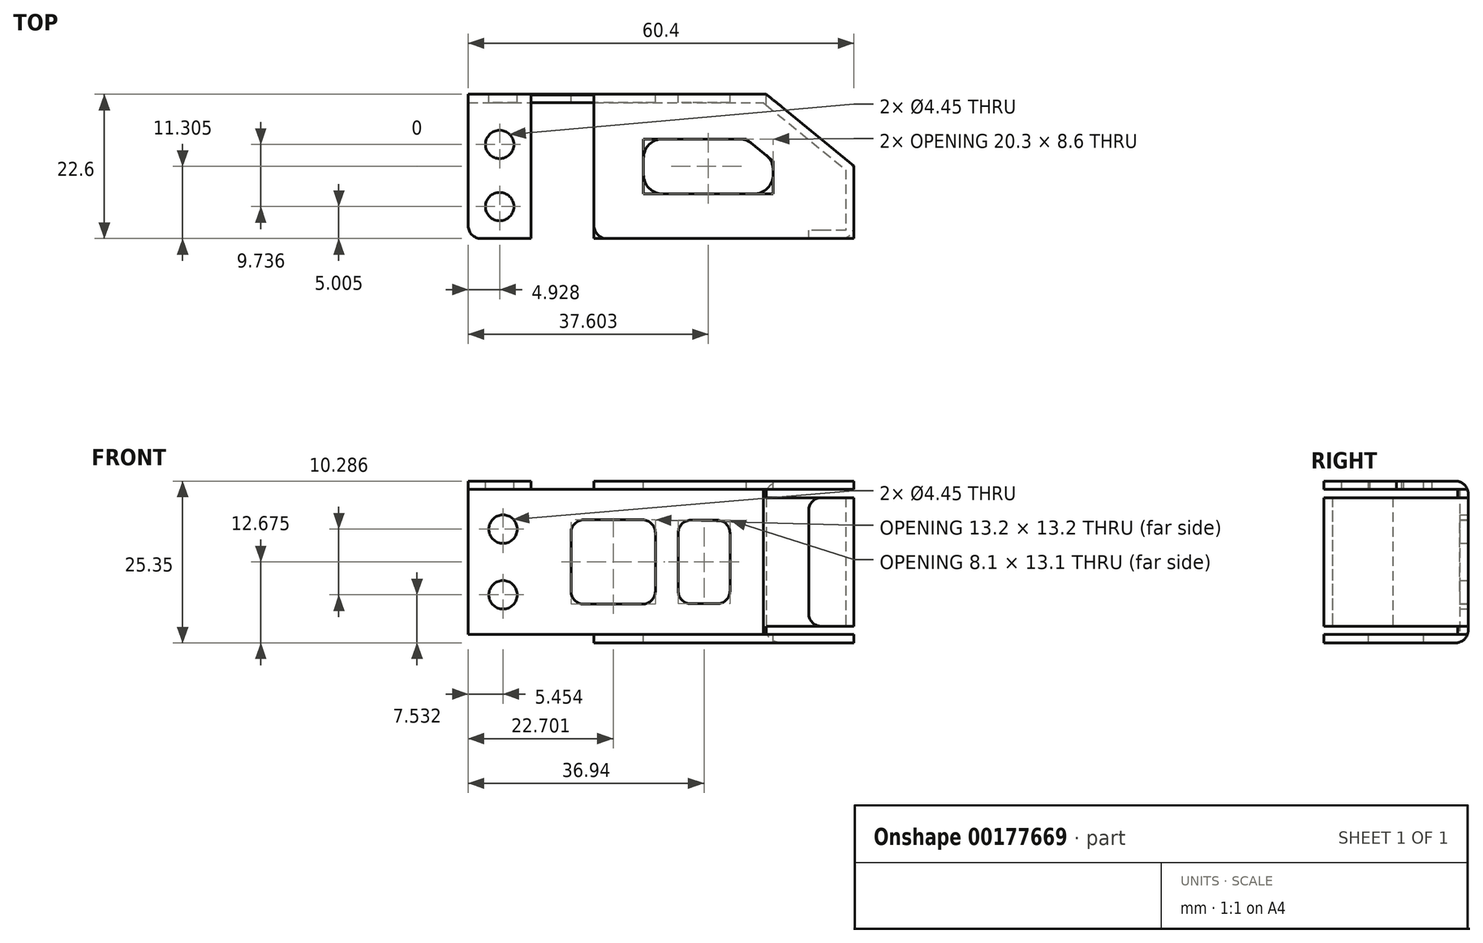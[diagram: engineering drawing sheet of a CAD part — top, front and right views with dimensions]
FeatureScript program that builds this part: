
annotation { "Feature Type Name" : "Feature", "Feature Type Description" : "" }
export const myFeature = defineFeature(function(context is Context, id is Id, definition is map)
    precondition{}
    {
        {
            var Q0;
            Q0=qCreatedBy(makeId("Top.planeOp"),FACE);
            var sketch = newSketch(context, id + "F0", { "sketchPlane" : qUnion([Q0])});
            skLineSegment(sketch, "E0.bottom", {"start": v(-31.59, -12.14) * mm, "end": v(13.31, -12.14) * mm});
            skLineSegment(sketch, "E0.top", {"start": v(-31.59, -33.44) * mm, "end": v(26.21, -33.44) * mm});
            skLineSegment(sketch, "E0.left", {"start": v(-31.59, -12.14) * mm, "end": v(-31.59, -33.44) * mm});
            skLineSegment(sketch, "E0.right", {"start": v(26.21, -22.66) * mm, "end": v(26.21, -33.44) * mm});
            skLineSegment(sketch, "E1", {"start": v(13.31, -12.14) * mm, "end": v(26.21, -22.66) * mm});
            skSolve(sketch);
        }
        {
            var Q0;
            Q0=makeQuery(id+"F0.imprint","IMPRINT",FACE,{"disambiguationData":[TD([[makeQuery(id+"F0.imprint","IMPRINT",EDGE,{"derivedFrom":sQuery(id+"F0.wireOp",EDGE,"E0.bottom")}),-1.0]])]});
            extrude(context, id + "F1", {"entities" : qUnion([Q0]), "depth" : 22.75 * mm});
        }
        {
            var Q0;
            Q0=makeQuery(id+"F1.opExtrude","SWEPT_FACE",FACE,{"disambiguationData":[OSD([sQuery(id+"F0.wireOp",EDGE,"E0.top")])]});
            shell(context, id + "F2", {"entities" : qUnion([Q0]), "thickness" : 1.3 * mm, "oppositeDirection" : true});
        }
        {
            var Q0;
            Q0=makeQuery(id+"F1.opExtrude","SWEPT_FACE",FACE,{"disambiguationData":[OSD([sQuery(id+"F0.wireOp",EDGE,"E0.left")])]});
            var sketch = newSketch(context, id + "F3", { "sketchPlane" : qUnion([Q0])});
            skLineSegment(sketch, "E2", {"start": v(12.14, -1.3) * mm, "end": v(12.14, 22.75) * mm});
            skLineSegment(sketch, "E3", {"start": v(12.14, 22.75) * mm, "end": v(33.44, 22.75) * mm});
            skSolve(sketch);
        }
        {
            var Q0;
            {var subQ0=sQuery(id+"F3.wireOp",EDGE,"E2");Q0=makeQuery(id+"F3.imprint","IMPRINT",FACE,{"disambiguationData":[TD([[makeQuery(id+"F3.imprint","IMPRINT",EDGE,{"derivedFrom":subQ0}),-1.0]])]});}
            extrude(context, id + "F4", {"entities" : qUnion([Q0]), "operationType" : NewBodyOperationType.REMOVE, "oppositeDirection" : true, "depth" : 19.7 * mm});
        }
        {
            var Q0;
            Q0=makeQuery(id+"F1.opExtrude","CAP_FACE",FACE,{"disambiguationData":[OSD([sQuery(id+"F0.wireOp",EDGE,"E0.bottom"),sQuery(id+"F0.wireOp",EDGE,"E0.top"),sQuery(id+"F0.wireOp",EDGE,"E0.left"),sQuery(id+"F0.wireOp",EDGE,"E0.right"),sQuery(id+"F0.wireOp",EDGE,"E1")])],"isStart":false});
            var sketch = newSketch(context, id + "F5", { "sketchPlane" : qUnion([Q0])});
            skLineSegment(sketch, "E4", {"start": v(-13.19, -12.14) * mm, "end": v(-13.19, -33.44) * mm});
            skLineSegment(sketch, "E5", {"start": v(-23.04, -33.44) * mm, "end": v(-23.04, -12.14) * mm});
            skLineSegment(sketch, "E6", {"start": v(-13.19, -33.44) * mm, "end": v(-32.89, -33.44) * mm});
            skLineSegment(sketch, "E7", {"start": v(-32.89, -33.44) * mm, "end": v(-23.04, -33.44) * mm});
            skLineSegment(sketch, "E8", {"start": v(-23.04, -12.14) * mm, "end": v(-32.89, -12.14) * mm});
            skLineSegment(sketch, "E9", {"start": v(-23.04, -12.14) * mm, "end": v(-23.04, -10.84) * mm});
            skLineSegment(sketch, "E10", {"start": v(-13.19, -12.14) * mm, "end": v(-13.19, -10.84) * mm});
            skSolve(sketch);
        }
        {
            var Q0;
            Q0=makeQuery(id+"F5.imprint","IMPRINT",FACE,{"disambiguationData":[TD([[makeQuery(id+"F5.imprint","IMPRINT",EDGE,{"derivedFrom":sQuery(id+"F5.wireOp",EDGE,"E4")}),-1.0]])]});
            extrude(context, id + "F6", {"entities" : qUnion([Q0]), "operationType" : NewBodyOperationType.REMOVE, "oppositeDirection" : true, "depth" : 1.3 * mm});
        }
        {
            var Q0;
            {var subQ0=sQuery(id+"F0.wireOp",EDGE,"E1");var subQ1=sQuery(id+"F0.wireOp",EDGE,"E0.top");var subQ2=sQuery(id+"F0.wireOp",EDGE,"E0.right");var subQ3=sQuery(id+"F0.wireOp",EDGE,"E0.bottom");Q0=makeQuery(id+"F6.boolean.opBoolean","SPLIT",FACE,{"disambiguationData":[TD([makeQuery(id+"F1.opExtrude","SWEPT_FACE",FACE,{"disambiguationData":[OSD([subQ2])]})])],"derivedFrom":makeQuery(id+"F1.opExtrude","CAP_FACE",FACE,{"disambiguationData":[OSD([subQ3,subQ1,sQuery(id+"F0.wireOp",EDGE,"E0.left"),subQ2,subQ0])],"isStart":false})});}
            var sketch = newSketch(context, id + "F7", { "sketchPlane" : qUnion([Q0])});
            skLineSegment(sketch, "E11", {"start": v(-5.44, -17.84) * mm, "end": v(10.65, -17.84) * mm});
            skLineSegment(sketch, "E12", {"start": v(10.65, -17.84) * mm, "end": v(14.86, -21.27) * mm});
            skLineSegment(sketch, "E13", {"start": v(14.86, -21.27) * mm, "end": v(14.86, -26.44) * mm});
            skLineSegment(sketch, "E14", {"start": v(14.86, -26.44) * mm, "end": v(-5.44, -26.44) * mm});
            skLineSegment(sketch, "E15", {"start": v(-5.44, -26.44) * mm, "end": v(-5.44, -17.84) * mm});
            skSolve(sketch);
        }
        {
            var Q0;
            Q0=makeQuery(id+"F7.imprint","IMPRINT",FACE,{"disambiguationData":[TD([[makeQuery(id+"F7.imprint","IMPRINT",EDGE,{"derivedFrom":sQuery(id+"F7.wireOp",EDGE,"E11")}),-1.0]])]});
            extrude(context, id + "F8", {"entities" : qUnion([Q0]), "operationType" : NewBodyOperationType.REMOVE, "oppositeDirection" : true, "depth" : 61.35 * mm});
        }
        {
            var Q0;
            Q0=makeQuery(id+"F1.opExtrude","SWEPT_FACE",FACE,{"disambiguationData":[OSD([sQuery(id+"F0.wireOp",EDGE,"E0.bottom")])]});
            var sketch = newSketch(context, id + "F9", { "sketchPlane" : qUnion([Q0])});
            skLineSegment(sketch, "E16.bottom", {"start": v(-8.1, 4.82) * mm, "end": v(0, 4.82) * mm});
            skLineSegment(sketch, "E16.top", {"start": v(-8.1, 17.93) * mm, "end": v(0, 17.93) * mm});
            skLineSegment(sketch, "E16.left", {"start": v(-8.1, 4.82) * mm, "end": v(-8.1, 17.93) * mm});
            skLineSegment(sketch, "E16.right", {"start": v(0, 4.82) * mm, "end": v(0, 17.93) * mm});
            skLineSegment(sketch, "E17.bottom", {"start": v(3.59, 4.77) * mm, "end": v(16.79, 4.77) * mm});
            skLineSegment(sketch, "E17.top", {"start": v(3.59, 17.97) * mm, "end": v(16.79, 17.97) * mm});
            skLineSegment(sketch, "E17.left", {"start": v(3.59, 4.77) * mm, "end": v(3.59, 17.98) * mm});
            skLineSegment(sketch, "E17.right", {"start": v(16.79, 4.77) * mm, "end": v(16.79, 17.97) * mm});
            skLineSegment(sketch, "E18", {"start": v(27.44, -1.3) * mm, "end": v(27.44, 24.05) * mm, "construction": true});
            skLineSegment(sketch, "E19", {"start": v(-13.78, 11.38) * mm, "end": v(32.89, 11.38) * mm, "construction": true});
            skCircle(sketch, "E20", {"center": v(27.44, 16.52) * mm, "radius": 2.23 * mm});
            skCircle(sketch, "E21", {"center": v(27.44, 6.23) * mm, "radius": 2.23 * mm});
            skLineSegment(sketch, "E22", {"start": v(27.44, 14.3) * mm, "end": v(27.44, 11.38) * mm});
            skLineSegment(sketch, "E23", {"start": v(27.44, 11.38) * mm, "end": v(27.44, 8.46) * mm});
            skLineSegment(sketch, "E24", {"start": v(13.19, -1.3) * mm, "end": v(13.19, 0) * mm});
            skLineSegment(sketch, "E25", {"start": v(13.19, 0) * mm, "end": v(32.89, 0) * mm});
            skPoint(sketch, "E26", {"position": v(16.79, 11.37) * mm});
            skPoint(sketch, "E27", {"position": v(0, 11.37) * mm});
            skSolve(sketch);
        }
        {
            var Q0;
            Q0=makeQuery(id+"F9.imprint","IMPRINT",FACE,{"disambiguationData":[TD([[makeQuery(id+"F9.imprint","IMPRINT",EDGE,{"derivedFrom":sQuery(id+"F9.wireOp",EDGE,"E16.bottom")}),1.0]])]});
            var Q1;
            Q1=makeQuery(id+"F9.imprint","IMPRINT",FACE,{"disambiguationData":[TD([[makeQuery(id+"F9.imprint","IMPRINT",EDGE,{"derivedFrom":sQuery(id+"F9.wireOp",EDGE,"E17.bottom")}),1.0]])]});
            var Q2;
            {var subQ0=sQuery(id+"F9.wireOp",EDGE,"E24");Q2=makeQuery(id+"F9.imprint","IMPRINT",FACE,{"disambiguationData":[TD([[makeQuery(id+"F9.imprint","IMPRINT",EDGE,{"derivedFrom":subQ0}),-1.0]])]});}
            var Q3;
            Q3=makeQuery(id+"F9.imprint","IMPRINT",FACE,{"disambiguationData":[TD([[makeQuery(id+"F9.imprint","IMPRINT",EDGE,{"derivedFrom":sQuery(id+"F9.wireOp",EDGE,"E21")}),1.0]])]});
            var Q4;
            Q4=makeQuery(id+"F9.imprint","IMPRINT",FACE,{"disambiguationData":[TD([[makeQuery(id+"F9.imprint","IMPRINT",EDGE,{"derivedFrom":sQuery(id+"F9.wireOp",EDGE,"E20")}),1.0]])]});
            extrude(context, id + "F10", {"entities" : qUnion([Q0, Q1, Q2, Q3, Q4]), "operationType" : NewBodyOperationType.REMOVE, "oppositeDirection" : true, "depth" : 25 * mm});
        }
        {
            var Q0;
            Q0=makeQuery(id+"F2.opShell","OFFSET_FACE",FACE,{"disambiguationData":[OSD([sQuery(id+"F0.wireOp",EDGE,"E0.right")])]});
            var sketch = newSketch(context, id + "F11", { "sketchPlane" : qUnion([Q0])});
            skLineSegment(sketch, "E28", {"start": v(32.14, 22.75) * mm, "end": v(32.14, 0) * mm});
            skSolve(sketch);
        }
        {
            var Q0;
            {var subQ0=sQuery(id+"F11.wireOp",EDGE,"E28");Q0=makeQuery(id+"F11.imprint","IMPRINT",FACE,{"disambiguationData":[TD([[makeQuery(id+"F11.imprint","IMPRINT",EDGE,{"derivedFrom":subQ0}),1.0]])]});}
            extrude(context, id + "F12", {"entities" : qUnion([Q0]), "operationType" : NewBodyOperationType.ADD, "depth" : 5.8 * mm});
        }
        {
            var Q0;
            Q0=makeQuery(id+"F1.opExtrude","SWEPT_FACE",FACE,{"disambiguationData":[OSD([sQuery(id+"F0.wireOp",EDGE,"E0.bottom")])]});
            var sketch = newSketch(context, id + "F13", { "sketchPlane" : qUnion([Q0])});
            skLineSegment(sketch, "E29", {"start": v(-13.78, 0) * mm, "end": v(-36.67, 0) * mm});
            skLineSegment(sketch, "E30", {"start": v(-13.78, 22.75) * mm, "end": v(-38.37, 22.75) * mm});
            skLineSegment(sketch, "E31", {"start": v(-13.78, 1.3) * mm, "end": v(-36.66, 1.3) * mm});
            skLineSegment(sketch, "E32", {"start": v(-13.78, 21.45) * mm, "end": v(-38.37, 21.45) * mm});
            skLineSegment(sketch, "E33", {"start": v(-36.67, 0) * mm, "end": v(-36.66, 1.3) * mm});
            skLineSegment(sketch, "E34", {"start": v(-38.37, 21.45) * mm, "end": v(-38.37, 22.75) * mm});
            skSolve(sketch);
        }
        {
            var Q0;
            {var subQ0=sQuery(id+"F13.wireOp",EDGE,"E29");Q0=makeQuery(id+"F13.imprint","IMPRINT",FACE,{"disambiguationData":[TD([[makeQuery(id+"F13.imprint","IMPRINT",EDGE,{"derivedFrom":subQ0}),-1.0]])]});}
            var Q1;
            {var subQ0=sQuery(id+"F13.wireOp",EDGE,"E30");Q1=makeQuery(id+"F13.imprint","IMPRINT",FACE,{"disambiguationData":[TD([[makeQuery(id+"F13.imprint","IMPRINT",EDGE,{"derivedFrom":subQ0}),1.0]])]});}
            extrude(context, id + "F14", {"entities" : qUnion([Q0, Q1]), "operationType" : NewBodyOperationType.REMOVE, "oppositeDirection" : true, "depth" : 25 * mm});
        }
        {
            var Q0;
            Q0=makeQuery(id+"F4.boolean.opBoolean","COPY",EDGE,{"derivedFrom":makeQuery(id+"F4.opExtrude","CAP_EDGE",EDGE,{"disambiguationData":[OSD([sQuery(id+"F0.wireOp",EDGE,"E0.top"),sQuery(id+"F0.wireOp",EDGE,"E0.left")])],"isStart":false})});
            var Q1;
            {var subQ0=sQuery(id+"F0.wireOp",EDGE,"E0.right");var subQ1=sQuery(id+"F0.wireOp",EDGE,"E0.top");Q1=makeQuery(id+"F14.boolean.opBoolean","SPLIT",EDGE,{"disambiguationData":[TD([makeQuery(id+"F14.opExtrude","SWEPT_FACE",FACE,{"disambiguationData":[OSD([sQuery(id+"F13.wireOp",EDGE,"E31")])]})])],"derivedFrom":makeQuery(id+"F1.opExtrude","SWEPT_EDGE",EDGE,{"disambiguationData":[OSD([subQ1,subQ0])]})});}
            var Q2;
            {var subQ1=sQuery(id+"F0.wireOp",EDGE,"E0.right");var subQ3=sQuery(id+"F0.wireOp",EDGE,"E0.top");Q2=makeQuery(id+"F14.boolean.opBoolean","SPLIT",EDGE,{"disambiguationData":[TD([makeQuery(id+"F14.opExtrude","SWEPT_FACE",FACE,{"disambiguationData":[OSD([sQuery(id+"F13.wireOp",EDGE,"E29")])]})])],"derivedFrom":makeQuery(id+"F1.opExtrude","SWEPT_EDGE",EDGE,{"disambiguationData":[OSD([subQ3,subQ1])]})});}
            var Q3;
            {var subQ1=sQuery(id+"F0.wireOp",EDGE,"E0.right");var subQ3=sQuery(id+"F0.wireOp",EDGE,"E0.top");Q3=makeQuery(id+"F14.boolean.opBoolean","SPLIT",EDGE,{"disambiguationData":[TD([makeQuery(id+"F4.opExtrude","SWEPT_FACE",FACE,{"disambiguationData":[OSD([sQuery(id+"F3.wireOp",EDGE,"E3")])]})])],"derivedFrom":makeQuery(id+"F1.opExtrude","SWEPT_EDGE",EDGE,{"disambiguationData":[OSD([subQ3,subQ1])]})});}
            var Q4;
            Q4=makeQuery(id+"F6.boolean.opBoolean","COPY",EDGE,{"derivedFrom":makeQuery(id+"F6.opExtrude","SWEPT_EDGE",EDGE,{"disambiguationData":[OSD([sQuery(id+"F0.wireOp",EDGE,"E0.top"),sQuery(id+"F5.wireOp",EDGE,"E4"),sQuery(id+"F5.wireOp",EDGE,"E6")])]})});
            var Q5;
            Q5=makeQuery(id+"F1.opExtrude","SWEPT_EDGE",EDGE,{"disambiguationData":[OSD([sQuery(id+"F0.wireOp",EDGE,"E0.top"),sQuery(id+"F0.wireOp",EDGE,"E0.left")])]});
            var Q6;
            Q6=makeQuery(id+"F6.boolean.opBoolean","COPY",EDGE,{"derivedFrom":makeQuery(id+"F6.opExtrude","SWEPT_EDGE",EDGE,{"disambiguationData":[OSD([sQuery(id+"F5.wireOp",EDGE,"E5"),sQuery(id+"F5.wireOp",EDGE,"E6"),sQuery(id+"F5.wireOp",EDGE,"E7")])]})});
            var Q7;
            Q7=makeQuery(id+"F10.boolean.opBoolean","COPY",EDGE,{"derivedFrom":makeQuery(id+"F10.opExtrude","SWEPT_EDGE",EDGE,{"disambiguationData":[OSD([sQuery(id+"F0.wireOp",EDGE,"E0.bottom"),sQuery(id+"F0.wireOp",EDGE,"E0.left"),sQuery(id+"F9.wireOp",EDGE,"E25")])]})});
            var Q8;
            Q8=makeQuery(id+"F14.boolean.opBoolean","INTERSECT",EDGE,{"derivedFrom":[makeQuery(id+"F12.opExtrude","CAP_FACE",FACE,{"disambiguationData":[OSD([sQuery(id+"F0.wireOp",EDGE,"E0.top"),sQuery(id+"F0.wireOp",EDGE,"E0.right"),sQuery(id+"F11.wireOp",EDGE,"E28")])],"isStart":false}),makeQuery(id+"F14.opExtrude","SWEPT_FACE",FACE,{"disambiguationData":[OSD([sQuery(id+"F13.wireOp",EDGE,"E31")])]})]});
            var Q9;
            Q9=makeQuery(id+"F14.boolean.opBoolean","INTERSECT",EDGE,{"derivedFrom":[makeQuery(id+"F12.opExtrude","CAP_FACE",FACE,{"disambiguationData":[OSD([sQuery(id+"F0.wireOp",EDGE,"E0.top"),sQuery(id+"F0.wireOp",EDGE,"E0.right"),sQuery(id+"F11.wireOp",EDGE,"E28")])],"isStart":false}),makeQuery(id+"F14.opExtrude","SWEPT_FACE",FACE,{"disambiguationData":[OSD([sQuery(id+"F13.wireOp",EDGE,"E32")])]})]});
            fillet(context, id + "F15", {"entities" : qUnion([Q0, Q1, Q2, Q3, Q4, Q5, Q6, Q7, Q8, Q9]), "radius" : 2 * mm, "tangentPropagation" : true, "allowEdgeOverflow" : false});
        }
        {
            var Q0;
            {var subQ0=sQuery(id+"F0.wireOp",EDGE,"E1");var subQ1=sQuery(id+"F0.wireOp",EDGE,"E0.right");var subQ2=sQuery(id+"F0.wireOp",EDGE,"E0.left");var subQ3=sQuery(id+"F0.wireOp",EDGE,"E0.top");var subQ4=sQuery(id+"F0.wireOp",EDGE,"E0.bottom");var subQ5=makeQuery(id+"F1.opExtrude","CAP_FACE",FACE,{"disambiguationData":[OSD([subQ4,subQ3,subQ2,subQ1,subQ0])],"isStart":true});var subQ6=sQuery(id+"F7.wireOp",EDGE,"E13");var subQ7=sQuery(id+"F7.wireOp",EDGE,"E12");Q0=makeQuery(id+"F8.boolean.opBoolean","COPY",EDGE,{"disambiguationData":[TD([subQ5])],"derivedFrom":makeQuery(id+"F8.opExtrude","SWEPT_EDGE",EDGE,{"disambiguationData":[OSD([subQ7,subQ6])]})});}
            var Q1;
            {var subQ0=sQuery(id+"F0.wireOp",EDGE,"E1");var subQ1=sQuery(id+"F0.wireOp",EDGE,"E0.right");var subQ2=sQuery(id+"F0.wireOp",EDGE,"E0.left");var subQ3=sQuery(id+"F0.wireOp",EDGE,"E0.top");var subQ4=sQuery(id+"F0.wireOp",EDGE,"E0.bottom");var subQ5=makeQuery(id+"F1.opExtrude","CAP_FACE",FACE,{"disambiguationData":[OSD([subQ4,subQ3,subQ2,subQ1,subQ0])],"isStart":true});var subQ6=sQuery(id+"F7.wireOp",EDGE,"E11");var subQ7=sQuery(id+"F7.wireOp",EDGE,"E12");Q1=makeQuery(id+"F8.boolean.opBoolean","COPY",EDGE,{"disambiguationData":[TD([subQ5])],"derivedFrom":makeQuery(id+"F8.opExtrude","SWEPT_EDGE",EDGE,{"disambiguationData":[OSD([subQ6,subQ7])]})});}
            var Q2;
            {var subQ0=sQuery(id+"F0.wireOp",EDGE,"E1");var subQ1=sQuery(id+"F0.wireOp",EDGE,"E0.right");var subQ2=sQuery(id+"F0.wireOp",EDGE,"E0.left");var subQ3=sQuery(id+"F0.wireOp",EDGE,"E0.top");var subQ4=sQuery(id+"F0.wireOp",EDGE,"E0.bottom");var subQ5=makeQuery(id+"F1.opExtrude","CAP_FACE",FACE,{"disambiguationData":[OSD([subQ4,subQ3,subQ2,subQ1,subQ0])],"isStart":true});var subQ6=sQuery(id+"F7.wireOp",EDGE,"E11");var subQ7=sQuery(id+"F7.wireOp",EDGE,"E15");Q2=makeQuery(id+"F8.boolean.opBoolean","COPY",EDGE,{"disambiguationData":[TD([subQ5])],"derivedFrom":makeQuery(id+"F8.opExtrude","SWEPT_EDGE",EDGE,{"disambiguationData":[OSD([subQ6,subQ7])]})});}
            var Q3;
            {var subQ0=sQuery(id+"F0.wireOp",EDGE,"E1");var subQ1=sQuery(id+"F0.wireOp",EDGE,"E0.right");var subQ2=sQuery(id+"F0.wireOp",EDGE,"E0.left");var subQ3=sQuery(id+"F0.wireOp",EDGE,"E0.top");var subQ4=sQuery(id+"F0.wireOp",EDGE,"E0.bottom");var subQ5=makeQuery(id+"F1.opExtrude","CAP_FACE",FACE,{"disambiguationData":[OSD([subQ4,subQ3,subQ2,subQ1,subQ0])],"isStart":true});var subQ6=sQuery(id+"F7.wireOp",EDGE,"E14");var subQ7=sQuery(id+"F7.wireOp",EDGE,"E15");Q3=makeQuery(id+"F8.boolean.opBoolean","COPY",EDGE,{"disambiguationData":[TD([subQ5])],"derivedFrom":makeQuery(id+"F8.opExtrude","SWEPT_EDGE",EDGE,{"disambiguationData":[OSD([subQ6,subQ7])]})});}
            var Q4;
            {var subQ0=sQuery(id+"F0.wireOp",EDGE,"E1");var subQ1=sQuery(id+"F0.wireOp",EDGE,"E0.right");var subQ2=sQuery(id+"F0.wireOp",EDGE,"E0.left");var subQ3=sQuery(id+"F0.wireOp",EDGE,"E0.top");var subQ4=sQuery(id+"F0.wireOp",EDGE,"E0.bottom");var subQ5=makeQuery(id+"F1.opExtrude","CAP_FACE",FACE,{"disambiguationData":[OSD([subQ4,subQ3,subQ2,subQ1,subQ0])],"isStart":true});var subQ6=sQuery(id+"F7.wireOp",EDGE,"E13");var subQ7=sQuery(id+"F7.wireOp",EDGE,"E14");Q4=makeQuery(id+"F8.boolean.opBoolean","COPY",EDGE,{"disambiguationData":[TD([subQ5])],"derivedFrom":makeQuery(id+"F8.opExtrude","SWEPT_EDGE",EDGE,{"disambiguationData":[OSD([subQ6,subQ7])]})});}
            var Q5;
            {var subQ0=sQuery(id+"F7.wireOp",EDGE,"E11");var subQ7=sQuery(id+"F7.wireOp",EDGE,"E12");Q5=makeQuery(id+"F8.boolean.opBoolean","COPY",EDGE,{"disambiguationData":[TD([makeQuery(id+"F4.opExtrude","SWEPT_FACE",FACE,{"disambiguationData":[OSD([sQuery(id+"F3.wireOp",EDGE,"E3")])]})])],"derivedFrom":makeQuery(id+"F8.opExtrude","SWEPT_EDGE",EDGE,{"disambiguationData":[OSD([subQ0,subQ7])]})});}
            var Q6;
            {var subQ0=sQuery(id+"F7.wireOp",EDGE,"E12");var subQ7=sQuery(id+"F7.wireOp",EDGE,"E13");Q6=makeQuery(id+"F8.boolean.opBoolean","COPY",EDGE,{"disambiguationData":[TD([makeQuery(id+"F4.opExtrude","SWEPT_FACE",FACE,{"disambiguationData":[OSD([sQuery(id+"F3.wireOp",EDGE,"E3")])]})])],"derivedFrom":makeQuery(id+"F8.opExtrude","SWEPT_EDGE",EDGE,{"disambiguationData":[OSD([subQ0,subQ7])]})});}
            var Q7;
            {var subQ0=sQuery(id+"F7.wireOp",EDGE,"E13");var subQ7=sQuery(id+"F7.wireOp",EDGE,"E14");Q7=makeQuery(id+"F8.boolean.opBoolean","COPY",EDGE,{"disambiguationData":[TD([makeQuery(id+"F4.opExtrude","SWEPT_FACE",FACE,{"disambiguationData":[OSD([sQuery(id+"F3.wireOp",EDGE,"E3")])]})])],"derivedFrom":makeQuery(id+"F8.opExtrude","SWEPT_EDGE",EDGE,{"disambiguationData":[OSD([subQ0,subQ7])]})});}
            var Q8;
            {var subQ0=sQuery(id+"F7.wireOp",EDGE,"E14");var subQ7=sQuery(id+"F7.wireOp",EDGE,"E15");Q8=makeQuery(id+"F8.boolean.opBoolean","COPY",EDGE,{"disambiguationData":[TD([makeQuery(id+"F4.opExtrude","SWEPT_FACE",FACE,{"disambiguationData":[OSD([sQuery(id+"F3.wireOp",EDGE,"E3")])]})])],"derivedFrom":makeQuery(id+"F8.opExtrude","SWEPT_EDGE",EDGE,{"disambiguationData":[OSD([subQ0,subQ7])]})});}
            var Q9;
            {var subQ0=sQuery(id+"F7.wireOp",EDGE,"E11");var subQ7=sQuery(id+"F7.wireOp",EDGE,"E15");Q9=makeQuery(id+"F8.boolean.opBoolean","COPY",EDGE,{"disambiguationData":[TD([makeQuery(id+"F4.opExtrude","SWEPT_FACE",FACE,{"disambiguationData":[OSD([sQuery(id+"F3.wireOp",EDGE,"E3")])]})])],"derivedFrom":makeQuery(id+"F8.opExtrude","SWEPT_EDGE",EDGE,{"disambiguationData":[OSD([subQ0,subQ7])]})});}
            fillet(context, id + "F16", {"entities" : qUnion([Q0, Q1, Q2, Q3, Q4, Q5, Q6, Q7, Q8, Q9]), "radius" : 3 * mm, "tangentPropagation" : true, "allowEdgeOverflow" : false});
        }
        {
            var Q0;
            {var subQ0=sQuery(id+"F0.wireOp",EDGE,"E0.bottom");var subQ1=sQuery(id+"F0.wireOp",EDGE,"E1");Q0=makeQuery(id+"F6.boolean.opBoolean","SPLIT",EDGE,{"disambiguationData":[TD([makeQuery(id+"F1.opExtrude","SWEPT_FACE",FACE,{"disambiguationData":[OSD([subQ1])]})])],"derivedFrom":makeQuery(id+"F1.opExtrude","CAP_EDGE",EDGE,{"disambiguationData":[OSD([subQ0])],"isStart":false})});}
            var Q1;
            {var subQ0=sQuery(id+"F0.wireOp",EDGE,"E0.bottom");var subQ1=sQuery(id+"F0.wireOp",EDGE,"E0.left");Q1=makeQuery(id+"F6.boolean.opBoolean","SPLIT",EDGE,{"disambiguationData":[TD([makeQuery(id+"F1.opExtrude","SWEPT_FACE",FACE,{"disambiguationData":[OSD([subQ1])]})])],"derivedFrom":makeQuery(id+"F1.opExtrude","CAP_EDGE",EDGE,{"disambiguationData":[OSD([subQ0])],"isStart":false})});}
            var Q2;
            Q2=makeQuery(id+"F1.opExtrude","CAP_EDGE",EDGE,{"disambiguationData":[OSD([sQuery(id+"F0.wireOp",EDGE,"E0.bottom")])],"isStart":true});
            var Q3;
            {var subQ0=sQuery(id+"F0.wireOp",EDGE,"E0.right");var subQ1=sQuery(id+"F0.wireOp",EDGE,"E1");Q3=makeQuery(id+"F14.boolean.opBoolean","SPLIT",EDGE,{"disambiguationData":[TD([makeQuery(id+"F14.opExtrude","SWEPT_FACE",FACE,{"disambiguationData":[OSD([sQuery(id+"F13.wireOp",EDGE,"E31")])]})])],"derivedFrom":makeQuery(id+"F1.opExtrude","SWEPT_EDGE",EDGE,{"disambiguationData":[OSD([subQ0,subQ1])]})});}
            var Q4;
            {var subQ0=sQuery(id+"F0.wireOp",EDGE,"E1");var subQ1=sQuery(id+"F0.wireOp",EDGE,"E0.right");Q4=makeQuery(id+"F14.boolean.opBoolean","SPLIT",EDGE,{"disambiguationData":[TD([makeQuery(id+"F4.opExtrude","SWEPT_FACE",FACE,{"disambiguationData":[OSD([sQuery(id+"F3.wireOp",EDGE,"E3")])]})])],"derivedFrom":makeQuery(id+"F1.opExtrude","SWEPT_EDGE",EDGE,{"disambiguationData":[OSD([subQ1,subQ0])]})});}
            var Q5;
            {var subQ0=sQuery(id+"F0.wireOp",EDGE,"E1");var subQ1=sQuery(id+"F0.wireOp",EDGE,"E0.right");Q5=makeQuery(id+"F14.boolean.opBoolean","SPLIT",EDGE,{"disambiguationData":[TD([makeQuery(id+"F14.opExtrude","SWEPT_FACE",FACE,{"disambiguationData":[OSD([sQuery(id+"F13.wireOp",EDGE,"E29")])]})])],"derivedFrom":makeQuery(id+"F1.opExtrude","SWEPT_EDGE",EDGE,{"disambiguationData":[OSD([subQ1,subQ0])]})});}
            fillet(context, id + "F17", {"entities" : qUnion([Q0, Q1, Q2, Q3, Q4, Q5]), "radius" : 2 * mm, "tangentPropagation" : true, "allowEdgeOverflow" : false});
        }
        {
            var Q0;
            Q0=makeQuery(id+"F10.boolean.opBoolean","COPY",EDGE,{"derivedFrom":makeQuery(id+"F10.opExtrude","SWEPT_EDGE",EDGE,{"disambiguationData":[OSD([sQuery(id+"F9.wireOp",EDGE,"E16.top"),sQuery(id+"F9.wireOp",EDGE,"E16.right")])]})});
            var Q1;
            Q1=makeQuery(id+"F10.boolean.opBoolean","COPY",EDGE,{"derivedFrom":makeQuery(id+"F10.opExtrude","SWEPT_EDGE",EDGE,{"disambiguationData":[OSD([sQuery(id+"F9.wireOp",EDGE,"E16.bottom"),sQuery(id+"F9.wireOp",EDGE,"E16.right")])]})});
            var Q2;
            Q2=makeQuery(id+"F10.boolean.opBoolean","COPY",EDGE,{"derivedFrom":makeQuery(id+"F10.opExtrude","SWEPT_EDGE",EDGE,{"disambiguationData":[OSD([sQuery(id+"F9.wireOp",EDGE,"E16.bottom"),sQuery(id+"F9.wireOp",EDGE,"E16.left")])]})});
            var Q3;
            Q3=makeQuery(id+"F10.boolean.opBoolean","COPY",EDGE,{"derivedFrom":makeQuery(id+"F10.opExtrude","SWEPT_EDGE",EDGE,{"disambiguationData":[OSD([sQuery(id+"F9.wireOp",EDGE,"E16.top"),sQuery(id+"F9.wireOp",EDGE,"E16.left")])]})});
            var Q4;
            Q4=makeQuery(id+"F10.boolean.opBoolean","COPY",EDGE,{"derivedFrom":makeQuery(id+"F10.opExtrude","SWEPT_EDGE",EDGE,{"disambiguationData":[OSD([sQuery(id+"F9.wireOp",EDGE,"E17.bottom"),sQuery(id+"F9.wireOp",EDGE,"E17.right")])]})});
            var Q5;
            Q5=makeQuery(id+"F10.boolean.opBoolean","COPY",EDGE,{"derivedFrom":makeQuery(id+"F10.opExtrude","SWEPT_EDGE",EDGE,{"disambiguationData":[OSD([sQuery(id+"F9.wireOp",EDGE,"E17.top"),sQuery(id+"F9.wireOp",EDGE,"E17.right")])]})});
            var Q6;
            Q6=makeQuery(id+"F10.boolean.opBoolean","COPY",EDGE,{"derivedFrom":makeQuery(id+"F10.opExtrude","SWEPT_EDGE",EDGE,{"disambiguationData":[OSD([sQuery(id+"F9.wireOp",EDGE,"E17.top"),sQuery(id+"F9.wireOp",EDGE,"E17.left")])]})});
            var Q7;
            Q7=makeQuery(id+"F10.boolean.opBoolean","COPY",EDGE,{"derivedFrom":makeQuery(id+"F10.opExtrude","SWEPT_EDGE",EDGE,{"disambiguationData":[OSD([sQuery(id+"F9.wireOp",EDGE,"E17.bottom"),sQuery(id+"F9.wireOp",EDGE,"E17.left")])]})});
            fillet(context, id + "F18", {"entities" : qUnion([Q0, Q1, Q2, Q3, Q4, Q5, Q6, Q7]), "radius" : 2 * mm, "tangentPropagation" : true, "allowEdgeOverflow" : false});
        }
        {
            var Q0;
            {var subQ0=sQuery(id+"F0.wireOp",EDGE,"E0.bottom");var subQ1=sQuery(id+"F0.wireOp",EDGE,"E0.top");var subQ2=sQuery(id+"F0.wireOp",EDGE,"E0.left");Q0=makeQuery(id+"F6.boolean.opBoolean","SPLIT",FACE,{"disambiguationData":[TD([makeQuery(id+"F1.opExtrude","SWEPT_FACE",FACE,{"disambiguationData":[OSD([subQ2])]})])],"derivedFrom":makeQuery(id+"F1.opExtrude","CAP_FACE",FACE,{"disambiguationData":[OSD([subQ0,subQ1,subQ2,sQuery(id+"F0.wireOp",EDGE,"E0.right"),sQuery(id+"F0.wireOp",EDGE,"E1")])],"isStart":false})});}
            var sketch = newSketch(context, id + "F19", { "sketchPlane" : qUnion([Q0])});
            skCircle(sketch, "E35", {"center": v(-27.96, -18.7) * mm, "radius": 2.23 * mm});
            skCircle(sketch, "E36", {"center": v(-27.96, -28.44) * mm, "radius": 2.23 * mm});
            skLineSegment(sketch, "E37", {"start": v(-27.96, -12.84) * mm, "end": v(-27.96, -33.44) * mm, "construction": true});
            skSolve(sketch);
        }
        {
            var Q0;
            Q0=qSketchRegion(id+"F19",true);
            extrude(context, id + "F20", {"entities" : qUnion([Q0]), "operationType" : NewBodyOperationType.REMOVE, "oppositeDirection" : true, "depth" : 25 * mm});
        }
    });
